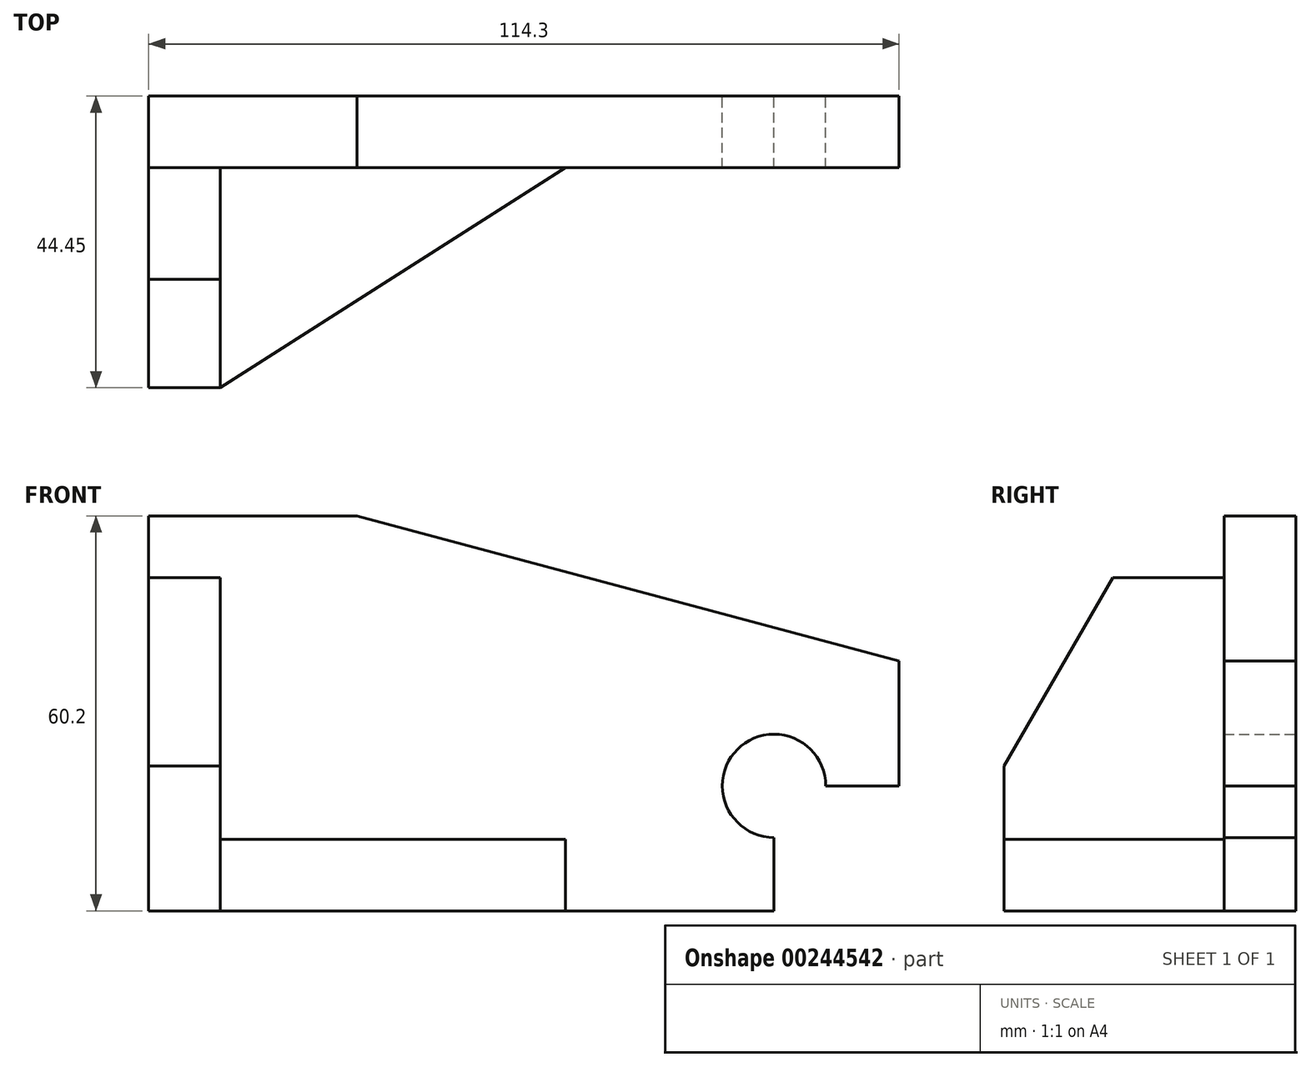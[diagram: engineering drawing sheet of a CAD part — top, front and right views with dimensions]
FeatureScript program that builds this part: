
annotation { "Feature Type Name" : "Feature", "Feature Type Description" : "" }
export const myFeature = defineFeature(function(context is Context, id is Id, definition is map)
    precondition{}
    {
        {
            var Q0;
            Q0=qCreatedBy(makeId("Front.planeOp"),FACE);
            var sketch = newSketch(context, id + "F0", { "sketchPlane" : qUnion([Q0])});
            skLineSegment(sketch, "E0.bottom", {"start": v(-57.15, 30.1) * mm, "end": v(57.15, 30.1) * mm});
            skLineSegment(sketch, "E0.top", {"start": v(-57.15, -30.1) * mm, "end": v(57.15, -30.1) * mm});
            skLineSegment(sketch, "E0.left", {"start": v(-57.15, 30.1) * mm, "end": v(-57.15, -30.1) * mm});
            skLineSegment(sketch, "E0.right", {"start": v(57.15, 30.1) * mm, "end": v(57.15, -30.1) * mm});
            skPoint(sketch, "E1", {"position": v(-25.4, 30.1) * mm});
            skLineSegment(sketch, "E2", {"start": v(-25.4, 30.1) * mm, "end": v(57.15, 7.98) * mm});
            skLineSegment(sketch, "E3", {"start": v(-57.15, 0) * mm, "end": v(57.15, 0) * mm});
            skLineSegment(sketch, "E4", {"start": v(0, 30.1) * mm, "end": v(0, -30.1) * mm});
            skLineSegment(sketch, "E5.bottom", {"start": v(57.15, -30.1) * mm, "end": v(38.1, -30.1) * mm});
            skLineSegment(sketch, "E5.top", {"start": v(57.15, -11.05) * mm, "end": v(38.1, -11.05) * mm});
            skLineSegment(sketch, "E5.left", {"start": v(57.15, -30.1) * mm, "end": v(57.15, -11.05) * mm});
            skLineSegment(sketch, "E5.right", {"start": v(38.1, -30.1) * mm, "end": v(38.1, -11.05) * mm});
            skCircle(sketch, "E6", {"center": v(38.1, -11.05) * mm, "radius": 7.87 * mm});
            skSolve(sketch);
        }
        {
            var Q0;
            {var subQ1=sQuery(id+"F0.wireOp",EDGE,"E0.left");var subQ5=sQuery(id+"F0.wireOp",EDGE,"E0.bottom");var subQ6=makeQuery(id+"F0.imprint","INTERSECT",VERTEX,{"derivedFrom":[subQ5,subQ1]});Q0=makeQuery(id+"F0.imprint","IMPRINT",FACE,{"disambiguationData":[TD([[makeQuery(id+"F0.imprint","IMPRINT",EDGE,{"disambiguationData":[TD([[subQ6,-1.0]])],"derivedFrom":subQ5}),-1.0]])]});}
            var Q1;
            {var subQ0=sQuery(id+"F0.wireOp",EDGE,"E2");var subQ1=sQuery(id+"F0.wireOp",EDGE,"E0.right");var subQ2=makeQuery(id+"F0.imprint","INTERSECT",VERTEX,{"derivedFrom":[subQ1,subQ0]});Q1=makeQuery(id+"F0.imprint","IMPRINT",FACE,{"disambiguationData":[TD([[makeQuery(id+"F0.imprint","IMPRINT",EDGE,{"disambiguationData":[TD([[subQ2,-1.0]])],"derivedFrom":subQ1}),-1.0]])]});}
            var Q2;
            {var subQ3=sQuery(id+"F0.wireOp",EDGE,"E3");var subQ5=sQuery(id+"F0.wireOp",EDGE,"E0.right");var subQ6=makeQuery(id+"F0.imprint","INTERSECT",VERTEX,{"derivedFrom":[subQ5,subQ3]});Q2=makeQuery(id+"F0.imprint","IMPRINT",FACE,{"disambiguationData":[TD([[makeQuery(id+"F0.imprint","IMPRINT",EDGE,{"disambiguationData":[TD([[subQ6,1.0]])],"derivedFrom":subQ3}),-1.0]])]});}
            var Q3;
            {var subQ0=sQuery(id+"F0.wireOp",EDGE,"E0.left");var subQ1=sQuery(id+"F0.wireOp",EDGE,"E0.top");var subQ2=makeQuery(id+"F0.imprint","INTERSECT",VERTEX,{"derivedFrom":[subQ1,subQ0]});Q3=makeQuery(id+"F0.imprint","IMPRINT",FACE,{"disambiguationData":[TD([[makeQuery(id+"F0.imprint","IMPRINT",EDGE,{"disambiguationData":[TD([[subQ2,-1.0]])],"derivedFrom":subQ1}),1.0]])]});}
            var Q4;
            {var subQ1=sQuery(id+"F0.wireOp",EDGE,"E5.bottom");Q4=makeQuery(id+"F0.imprint","IMPRINT",FACE,{"disambiguationData":[TD([[makeQuery(id+"F0.imprint","IMPRINT",EDGE,{"derivedFrom":subQ1}),-1.0]])]});}
            extrude(context, id + "F1", {"entities" : qUnion([Q0, Q1, Q2, Q3, Q4]), "depth" : 10.92 * mm});
        }
        {
            var Q0;
            Q0=makeQuery(id+"F1.opExtrude","CAP_FACE",FACE,{"disambiguationData":[OSD([sQuery(id+"F0.wireOp",EDGE,"E0.bottom"),sQuery(id+"F0.wireOp",EDGE,"E0.top"),sQuery(id+"F0.wireOp",EDGE,"E0.left"),sQuery(id+"F0.wireOp",EDGE,"E0.right"),sQuery(id+"F0.wireOp",EDGE,"E2"),sQuery(id+"F0.wireOp",EDGE,"E5.bottom"),sQuery(id+"F0.wireOp",EDGE,"E5.left"),sQuery(id+"F0.wireOp",EDGE,"E6")])],"isStart":false});
            var sketch = newSketch(context, id + "F2", { "sketchPlane" : qUnion([Q0])});
            skLineSegment(sketch, "E7.bottom", {"start": v(-57.15, -30.1) * mm, "end": v(-46.23, -30.1) * mm});
            skLineSegment(sketch, "E7.top", {"start": v(-57.15, 20.7) * mm, "end": v(-46.23, 20.7) * mm});
            skLineSegment(sketch, "E7.left", {"start": v(-57.15, -30.1) * mm, "end": v(-57.15, 20.7) * mm});
            skLineSegment(sketch, "E7.right", {"start": v(-46.23, -30.1) * mm, "end": v(-46.23, 20.7) * mm});
            skLineSegment(sketch, "E8.bottom", {"start": v(-46.23, -30.1) * mm, "end": v(6.35, -30.1) * mm});
            skLineSegment(sketch, "E8.top", {"start": v(-46.23, -19.18) * mm, "end": v(6.35, -19.18) * mm});
            skLineSegment(sketch, "E8.left", {"start": v(-46.23, -30.1) * mm, "end": v(-46.23, -19.18) * mm});
            skLineSegment(sketch, "E8.right", {"start": v(6.35, -30.1) * mm, "end": v(6.35, -19.18) * mm});
            skSolve(sketch);
        }
        {
            var Q0;
            Q0=makeQuery(id+"F2.imprint","IMPRINT",FACE,{"disambiguationData":[TD([[makeQuery(id+"F2.imprint","IMPRINT",EDGE,{"derivedFrom":sQuery(id+"F2.wireOp",EDGE,"E7.bottom")}),1.0]])]});
            var Q1;
            Q1=makeQuery(id+"F2.imprint","IMPRINT",FACE,{"disambiguationData":[TD([[makeQuery(id+"F2.imprint","IMPRINT",EDGE,{"derivedFrom":sQuery(id+"F2.wireOp",EDGE,"E8.bottom")}),1.0]])]});
            extrude(context, id + "F3", {"entities" : qUnion([Q0, Q1]), "operationType" : NewBodyOperationType.ADD, "depth" : 33.53 * mm});
        }
        {
            var Q0;
            Q0=makeQuery(id+"F3.opExtrude","SWEPT_FACE",FACE,{"disambiguationData":[OSD([sQuery(id+"F2.wireOp",EDGE,"E8.top")])]});
            var sketch = newSketch(context, id + "F4", { "sketchPlane" : qUnion([Q0])});
            skLineSegment(sketch, "E9", {"start": v(-46.23, -44.45) * mm, "end": v(6.35, -10.92) * mm});
            skSolve(sketch);
        }
        {
            var Q0;
            Q0=makeQuery(id+"F4.imprint","IMPRINT",FACE,{"disambiguationData":[TD([[makeQuery(id+"F4.imprint","IMPRINT",EDGE,{"derivedFrom":sQuery(id+"F4.wireOp",EDGE,"E9")}),-1.0]])]});
            extrude(context, id + "F5", {"entities" : qUnion([Q0]), "operationType" : NewBodyOperationType.REMOVE, "endBound" : BoundingType.THROUGH_ALL, "oppositeDirection" : true, "depth" : 25.4 * mm});
        }
        {
            var Q0;
            Q0=makeQuery(id+"F3.boolean.opBoolean","MERGE",FACE,{"derivedFrom":[makeQuery(id+"F1.opExtrude","SWEPT_FACE",FACE,{"disambiguationData":[OSD([sQuery(id+"F0.wireOp",EDGE,"E0.left")])]}),makeQuery(id+"F3.opExtrude","SWEPT_FACE",FACE,{"disambiguationData":[OSD([sQuery(id+"F2.wireOp",EDGE,"E7.left")])]})]});
            var sketch = newSketch(context, id + "F6", { "sketchPlane" : qUnion([Q0])});
            skPoint(sketch, "E10", {"position": v(44.45, -8) * mm});
            skLineSegment(sketch, "E11", {"start": v(44.45, -8) * mm, "end": v(27.88, 20.7) * mm});
            skSolve(sketch);
        }
        {
            var Q0;
            {var subQ0=sQuery(id+"F6.wireOp",EDGE,"E11");Q0=makeQuery(id+"F6.imprint","IMPRINT",FACE,{"disambiguationData":[TD([[makeQuery(id+"F6.imprint","IMPRINT",EDGE,{"derivedFrom":subQ0}),-1.0]])]});}
            extrude(context, id + "F7", {"entities" : qUnion([Q0]), "operationType" : NewBodyOperationType.REMOVE, "endBound" : BoundingType.THROUGH_ALL, "oppositeDirection" : true, "depth" : 25.4 * mm});
        }
    });
